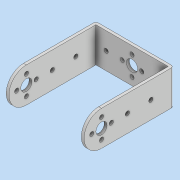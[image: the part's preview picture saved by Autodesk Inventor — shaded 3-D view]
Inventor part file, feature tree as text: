
AUTODESK INVENTOR PART (.ipt)
format: ipt  version: 2021.4 (Build 254397000, 397)  size: 196,608 bytes
history: native  units: in
note: dims shown in document units (in); Inventor stores cm internally (conversion verified against a paired STEP export)
features: sketch x5, extrude x5, hole x3, fillet x1
ambient origin geometry x8: Origin, YZ Plane, XZ Plane, XY Plane, X Axis, Y Axis, Z Axis, Center Point
bodies: Solid1 (feature_tree)
feature tree (14):
  sketch  "Sketch1"  dims[d0=2.0472in d1=0.9843in]
  extrude  "Extrusion1"  Depth=0.9843in
  extrude  "Extrusion2"  Depth=0.1181in
  extrude  "Extrusion3"  Depth=0.1181in
  extrude  "Extrusion4"  Depth=0.1181in
  extrude  "Extrusion5"  Depth=0.0787in
  fillet  "Fillet1"  Radius=1.0236in
  sketch  "Sketch5"  dims[d9=0.2913in d10=0.2913in d11=1.0236in d13=0.0787in d14=0.0787in d15=0.0787in d16=0.0in d17=0.1181in d18=0.0in d19=1.9291in d20=0.0in d22=0.4921in d23=0.0787in d24=0.0in d25=0.0787in d26=0.0in d27=0.0787in d28=0.315in d29=0.5512in d30=1.5748in d32=360.0deg d34=0.1181in d35=0.7323in d36=0.1181in d37=0.2362in d38=0.1575in d39=0.0787in d40=90.0deg d41=0.315in d42=0.8108in d43=0.315in d44=0.2362in d45=0.1575in d46=0.0787in d47=90.0deg d48=0.315in d49=0.8108in d50=0.1181in d51=0.6642in d52=0.1181in d53=0.2362in d54=0.1575in d55=0.0787in d56=90.0deg d57=0.315in d58=0.8108in]
  hole  "Hole1"  [1 undecoded]
  hole  "Hole2"  [1 undecoded]
  hole  "Hole3"  [1 undecoded]
  sketch  "Sketch2"  dims[d2=0.1181in d3=0.1181in]
  sketch  "Sketch3"  dims[d4=0.1181in d5=0.1181in]
  sketch  "Sketch4"  dims[d6=0.1181in d7=0.1181in]
note: 3 required parameter values undecoded (feature->parameter linkage not recoverable at this tier; creation-order binding heuristic only, values carry confidence <= 0.55)
